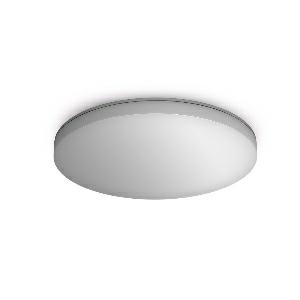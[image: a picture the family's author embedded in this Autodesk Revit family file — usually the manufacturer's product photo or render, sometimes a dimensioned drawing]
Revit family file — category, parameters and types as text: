
# Revit family: rs_pro_connect_r20_sl_057091
name_source: partatom
category: Leuchten
revit_build: Autodesk Revit 2016 (Build: 20190508_0715(x64)
units: mm (PartAtom-declared; Revit-internal decimal feet)

## family parameters
Basisbauteil = Fläche
Beim Laden mit Abzugskörper schneiden = Nein
Bemaßung runder Anschluss = Durchmesser verwenden
Gemeinsam genutzt = Nein
Lichtquelle = Nein
Raumberechnungspunkt = Nein
Teiletyp = Normal

## types (1)
- RS PRO Connect R20 SL (1 x , 1950 lm, 3000 K)
    Beschreibung = Dimensions (Ø x H): 350 x 55 mm; Mains power supply: 220 – 240 V / 50 – 60 Hz; Output: 16 W; Luminous flux: 1950 lm; Colour temperature: 3000 K; Colour variation LED: SDCM3; Colour Rendering Index CRI: 80-89; With lamp: Yes, STEINEL LED system; Lamp: LED cannot be replaced; LED life expectancy (max. °C): 50000 h; LED life expectancy (25 °C): 60000 h; Drop in luminous flux in accordance with LM80: L80B50; Base: without; LED cooling system: Passive Thermo Control; With motion detector: No; Main light adjustable: 50 - 100 %; Continuous light: selectable; Photo-cell controller: No; Basic light level function, detail: LED Backlight; Functions: Backlight; Soft light start: Yes; Impact resistance: IK07; IP-rating: IP40; Protection class: II; Ambient temperature: -20 – 40 °C; Housing material: Plastic; Cover material: PC, opal; Manufacturer's Warranty: 5 years; Settings via: Bluetooth; With remote control: No; Version: warm white; PU1, EAN: 4007841057091
    CIE Flux Codes = 44 75 94 95 100
    Color Rendering = 80-89
    Color Temperature = 3000 K
    Frequency = 60 Hz, 50 Hz
    Height = 0 mm  [stored 0 ft]
    Hersteller = Steinel
    Lamp Light Flux = 1950 lm
    Lamp count = 1
    Lampe = 1 x
    Length = 350 mm
    Luminous efficacy = 0 lm/W
    ModVariant = Nein
    Modell = 057091
    Mounting Type = Surface mounted
    Number of Poles = 1
    OnlyDefault = Ja
    Power Factor = 1
    Product Name = RS PRO Connect R20 SL
    Product group = Sensor-switched indoor light
    ProductGroupID = 30
    Protection Class = Protection class II
    Protection Degree = IP 40
    RlxData = <blob elided: 175569 chars, md5=c42ac630>
    Scheinlast = 0 VA
    Socket = socket
    Standby Power = 0 W
    System Light Flux = 0 lm
    System Power = 0 W
    Typenbild = produkt1_057091.jpg
    Typenkommentare = Product without accessories
    URL = http://relux.com
    VarID = ---
    Voltage = 0 V
    Vorgabe-Ansicht = 1800 mm
    Weight = 0.00 kg
    Width = 0 mm  [stored 0 ft]

note: [stored X ft] marks values corroborated as IEEE doubles in the binary element streams (Revit-internal decimal feet)

## geometry (parser evidence)
native form markers: Sweep x13
no freeform markers — native parametric forms only
